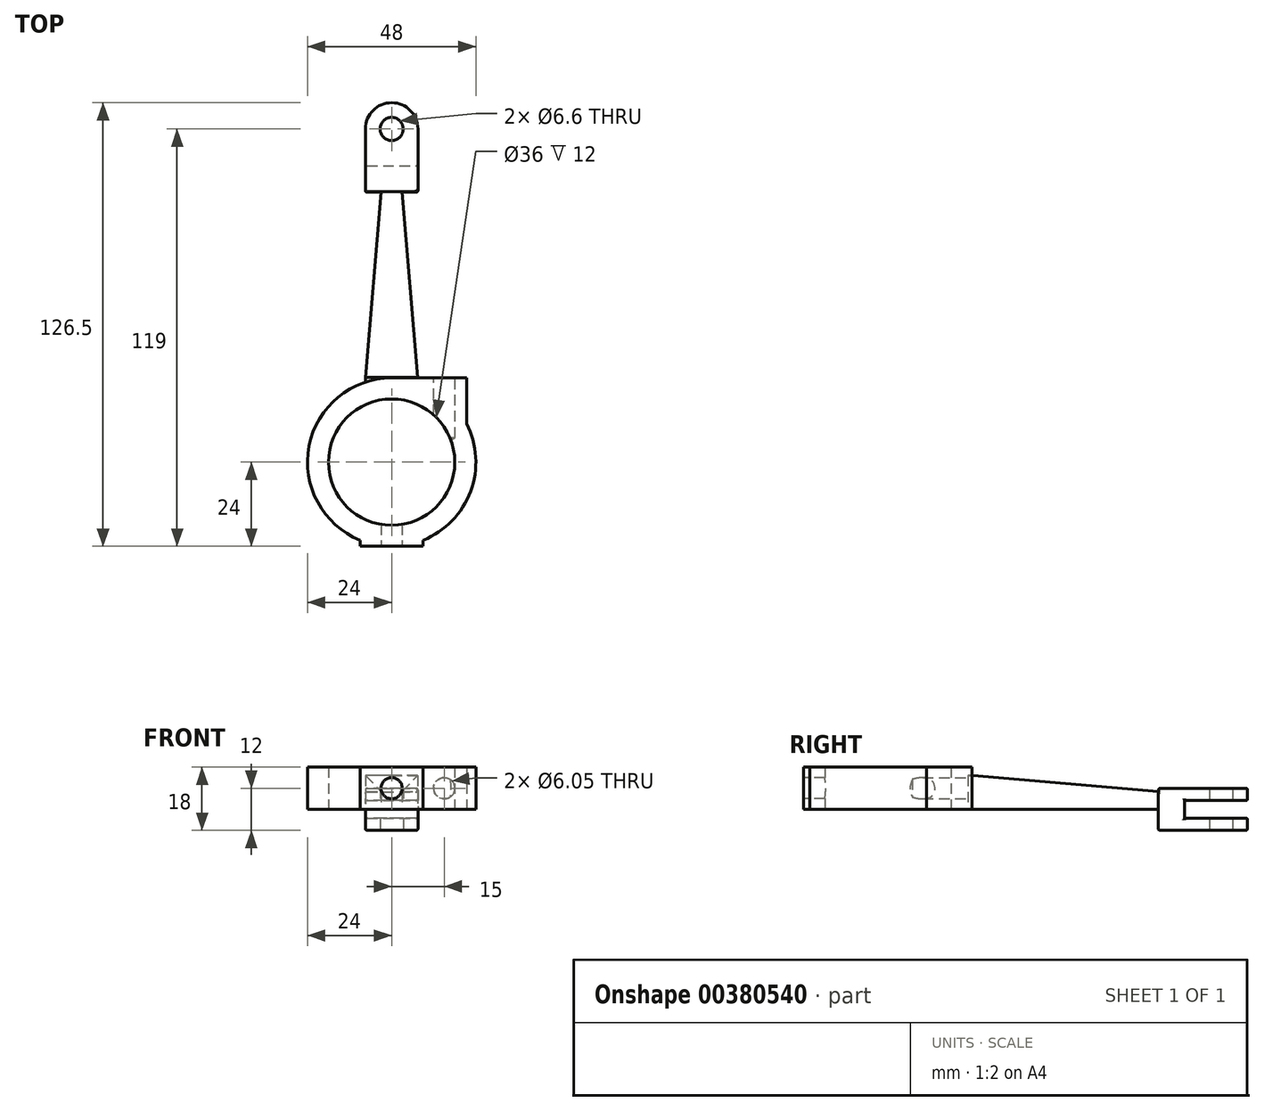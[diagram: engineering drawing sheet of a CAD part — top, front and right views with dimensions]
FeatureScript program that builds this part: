
annotation { "Feature Type Name" : "Feature", "Feature Type Description" : "" }
export const myFeature = defineFeature(function(context is Context, id is Id, definition is map)
    precondition{}
    {
        {
            var Q0;
            Q0=qCreatedBy(makeId("Top.planeOp"),FACE);
            var sketch = newSketch(context, id + "F0", { "sketchPlane" : qUnion([Q0])});
            skCircle(sketch, "E0", {"center": v(0, 0) * mm, "radius": 18 * mm});
            skArc(sketch, "E1", {"start": v(9, -22.25) * mm, "mid": v(22.5, -8.35) * mm, "end": v(21.33, 11) * mm});
            skLineSegment(sketch, "E2", {"start": v(-7.5, 22.8) * mm, "end": v(-3, 77) * mm});
            skLineSegment(sketch, "E3", {"start": v(3, 77) * mm, "end": v(7.4, 24) * mm});
            skLineSegment(sketch, "E4.bottom", {"start": v(-7.5, 95) * mm, "end": v(7.5, 95) * mm, "construction": true});
            skLineSegment(sketch, "E4.left", {"start": v(-7.5, 95) * mm, "end": v(-7.5, 77) * mm});
            skLineSegment(sketch, "E4.right", {"start": v(7.5, 95) * mm, "end": v(7.5, 77) * mm});
            skLineSegment(sketch, "E5", {"start": v(-7.5, 77) * mm, "end": v(-3, 77) * mm});
            skLineSegment(sketch, "E6", {"start": v(3, 77) * mm, "end": v(7.5, 77) * mm});
            skArc(sketch, "E7", {"start": v(7.5, 95) * mm, "mid": v(0, 102.5) * mm, "end": v(-7.5, 95) * mm});
            skCircle(sketch, "E8", {"center": v(0, 95) * mm, "radius": 3.3 * mm});
            skLineSegment(sketch, "E9", {"start": v(0, 24) * mm, "end": v(0, 77) * mm, "construction": true});
            skLineSegment(sketch, "E10", {"start": v(-7.5, 77) * mm, "end": v(7.5, 77) * mm});
            skLineSegment(sketch, "E11", {"start": v(0, 0) * mm, "end": v(0, 95) * mm, "construction": true});
            skLineSegment(sketch, "E12", {"start": v(-9, -22.25) * mm, "end": v(-9, -24) * mm});
            skLineSegment(sketch, "E13", {"start": v(9, -22.25) * mm, "end": v(9, -24) * mm});
            skLineSegment(sketch, "E14", {"start": v(21.33, 11) * mm, "end": v(21.33, 24) * mm});
            skLineSegment(sketch, "E15", {"start": v(21.33, 24) * mm, "end": v(7.4, 24) * mm});
            skLineSegment(sketch, "E16", {"start": v(-9, -24) * mm, "end": v(9, -24) * mm});
            skArc(sketch, "E17.trimOffspring", {"start": v(0, 24) * mm, "mid": v(-23.56, 4.58) * mm, "end": v(-9, -22.25) * mm});
            skLineSegment(sketch, "E18", {"start": v(0, 24) * mm, "end": v(7.4, 24) * mm});
            skSolve(sketch);
        }
        {
            var Q0;
            Q0=makeQuery(id+"F0.imprint","IMPRINT",FACE,{"disambiguationData":[TD([[makeQuery(id+"F0.imprint","IMPRINT",EDGE,{"derivedFrom":sQuery(id+"F0.wireOp",EDGE,"E0")}),-1.0]])]});
            extrude(context, id + "F1", {"entities" : qUnion([Q0]), "depth" : 12 * mm});
        }
        {
            var Q0;
            {var subQ1=sQuery(id+"F0.wireOp",EDGE,"E2");Q0=makeQuery(id+"F0.imprint","IMPRINT",FACE,{"disambiguationData":[TD([[makeQuery(id+"F0.imprint","IMPRINT",EDGE,{"derivedFrom":subQ1}),-1.0]])]});}
            extrude(context, id + "F2", {"entities" : qUnion([Q0]), "operationType" : NewBodyOperationType.ADD, "depth" : 9.6 * mm});
        }
        {
            var Q0;
            {var subQ1=sQuery(id+"F0.wireOp",EDGE,"E4.left");Q0=makeQuery(id+"F0.imprint","IMPRINT",FACE,{"disambiguationData":[TD([[makeQuery(id+"F0.imprint","IMPRINT",EDGE,{"derivedFrom":subQ1}),1.0]])]});}
            extrude(context, id + "F3", {"entities" : qUnion([Q0]), "operationType" : NewBodyOperationType.ADD, "depth" : 6 * mm, "hasSecondDirection" : true, "secondDirectionOppositeDirection" : true, "secondDirectionDepth" : 6 * mm});
        }
        {
            var Q0;
            Q0=qCreatedBy(makeId("Right.planeOp"),FACE);
            var sketch = newSketch(context, id + "F4", { "sketchPlane" : qUnion([Q0])});
            skLineSegment(sketch, "E19", {"start": v(77.12, 5) * mm, "end": v(24.03, 9.61) * mm});
            skLineSegment(sketch, "E20", {"start": v(24.03, 9.61) * mm, "end": v(77.12, 9.61) * mm});
            skLineSegment(sketch, "E21", {"start": v(77.12, 9.61) * mm, "end": v(77.12, 5) * mm});
            skSolve(sketch);
        }
        {
            var Q0;
            Q0=qSketchRegion(id+"F4",true);
            extrude(context, id + "F5", {"entities" : qUnion([Q0]), "operationType" : NewBodyOperationType.REMOVE, "oppositeDirection" : true, "depth" : 25 * mm, "hasSecondDirection" : true, "secondDirectionOppositeDirection" : false, "secondDirectionDepth" : 25 * mm});
        }
        {
            var Q0;
            Q0=makeQuery(id+"F3.opExtrude","SWEPT_FACE",FACE,{"disambiguationData":[OSD([sQuery(id+"F0.wireOp",EDGE,"E4.right")])]});
            var sketch = newSketch(context, id + "F6", { "sketchPlane" : qUnion([Q0])});
            skLineSegment(sketch, "E22.bottom", {"start": v(102.5, -2.5) * mm, "end": v(84.5, -2.5) * mm});
            skLineSegment(sketch, "E22.top", {"start": v(102.5, 2.5) * mm, "end": v(84.5, 2.5) * mm});
            skLineSegment(sketch, "E22.left", {"start": v(102.5, -2.5) * mm, "end": v(102.5, 2.5) * mm});
            skLineSegment(sketch, "E22.right", {"start": v(84.5, -2.5) * mm, "end": v(84.5, 2.5) * mm});
            skPoint(sketch, "E22.middle", {"position": v(93.5, 0) * mm});
            skSolve(sketch);
        }
        {
            var Q0;
            {var subQ0=sQuery(id+"F6.wireOp",EDGE,"E22.right");Q0=makeQuery(id+"F6.imprint","IMPRINT",FACE,{"disambiguationData":[TD([[makeQuery(id+"F6.imprint","IMPRINT",EDGE,{"derivedFrom":subQ0}),-1.0]])]});}
            var Q1;
            {var subQ0=sQuery(id+"F6.wireOp",EDGE,"E22.left");Q1=makeQuery(id+"F6.imprint","IMPRINT",FACE,{"disambiguationData":[TD([[makeQuery(id+"F6.imprint","IMPRINT",EDGE,{"derivedFrom":subQ0}),1.0]])]});}
            extrude(context, id + "F7", {"entities" : qUnion([Q0, Q1]), "operationType" : NewBodyOperationType.REMOVE, "oppositeDirection" : true, "depth" : 25 * mm});
        }
        {
            var Q0;
            Q0=makeQuery(id+"F1.opExtrude","SWEPT_FACE",FACE,{"disambiguationData":[OSD([sQuery(id+"F0.wireOp",EDGE,"E16")])]});
            var sketch = newSketch(context, id + "F8", { "sketchPlane" : qUnion([Q0])});
            skLineSegment(sketch, "E23", {"start": v(0, 0) * mm, "end": v(0, 12) * mm, "construction": true});
            skLineSegment(sketch, "E24", {"start": v(9, 6) * mm, "end": v(-9, 6) * mm, "construction": true});
            skPoint(sketch, "E25", {"position": v(0, 6) * mm});
            skSolve(sketch);
        }
        {
            var Q0;
            Q0=sQuery(id+"F8.wireOp",VERTEX,"E25");
            var Q1;
            Q1=makeQuery(id+"F1.opExtrude","SWEPT_BODY",BODY,{"disambiguationData":[OSD([sQuery(id+"F0.wireOp",EDGE,"E0"),sQuery(id+"F0.wireOp",EDGE,"E1"),sQuery(id+"F0.wireOp",EDGE,"E12"),sQuery(id+"F0.wireOp",EDGE,"E13"),sQuery(id+"F0.wireOp",EDGE,"E14"),sQuery(id+"F0.wireOp",EDGE,"E15"),sQuery(id+"F0.wireOp",EDGE,"E16"),sQuery(id+"F0.wireOp",EDGE,"E17.trimOffspring"),sQuery(id+"F0.wireOp",EDGE,"E18")])]});
            hole(context, id + "F9", {"style" : HoleStyle.SIMPLE, "endStyle" : HoleEndStyle.BLIND, "holeDiameter" : 5 * mm, "holeDepth" : 17 * mm, "tappedDepth" : 12.7 * mm, "tapClearance" : 3, "locations" : qUnion([Q0]), "scope" : qUnion([Q1])});
        }
        {
            var Q0;
            Q0=makeQuery(id+"F1.opExtrude","SWEPT_FACE",FACE,{"disambiguationData":[OSD([sQuery(id+"F0.wireOp",EDGE,"E15"),sQuery(id+"F0.wireOp",EDGE,"E18")])]});
            var sketch = newSketch(context, id + "F10", { "sketchPlane" : qUnion([Q0])});
            skLineSegment(sketch, "E26", {"start": v(-21.33, 6) * mm, "end": v(0, 6) * mm, "construction": true});
            skLineSegment(sketch, "E27", {"start": v(-15, 21.84) * mm, "end": v(-15, -13.14) * mm, "construction": true});
            skPoint(sketch, "E28", {"position": v(-15, 6) * mm});
            skSolve(sketch);
        }
        {
            var Q0;
            Q0=sQuery(id+"F10.wireOp",VERTEX,"E28");
            var Q1;
            Q1=makeQuery(id+"F1.opExtrude","SWEPT_BODY",BODY,{"disambiguationData":[OSD([sQuery(id+"F0.wireOp",EDGE,"E0"),sQuery(id+"F0.wireOp",EDGE,"E1"),sQuery(id+"F0.wireOp",EDGE,"E12"),sQuery(id+"F0.wireOp",EDGE,"E13"),sQuery(id+"F0.wireOp",EDGE,"E14"),sQuery(id+"F0.wireOp",EDGE,"E15"),sQuery(id+"F0.wireOp",EDGE,"E16"),sQuery(id+"F0.wireOp",EDGE,"E17.trimOffspring"),sQuery(id+"F0.wireOp",EDGE,"E18")])]});
            hole(context, id + "F11", {"style" : HoleStyle.SIMPLE, "endStyle" : HoleEndStyle.BLIND, "holeDiameter" : 5 * mm, "holeDepth" : 17 * mm, "tappedDepth" : 12.7 * mm, "tapClearance" : 3, "locations" : qUnion([Q0]), "scope" : qUnion([Q1])});
        }
        {
            var Q0;
            Q0=sQuery(id+"F10.wireOp",VERTEX,"E28");
            var Q1;
            Q1=makeQuery(id+"F1.opExtrude","SWEPT_BODY",BODY,{"disambiguationData":[OSD([sQuery(id+"F0.wireOp",EDGE,"E0"),sQuery(id+"F0.wireOp",EDGE,"E1"),sQuery(id+"F0.wireOp",EDGE,"E12"),sQuery(id+"F0.wireOp",EDGE,"E13"),sQuery(id+"F0.wireOp",EDGE,"E14"),sQuery(id+"F0.wireOp",EDGE,"E15"),sQuery(id+"F0.wireOp",EDGE,"E16"),sQuery(id+"F0.wireOp",EDGE,"E17.trimOffspring"),sQuery(id+"F0.wireOp",EDGE,"E18")])]});
            hole(context, id + "F12", {"style" : HoleStyle.SIMPLE, "endStyle" : HoleEndStyle.BLIND, "holeDiameter" : 6.05 * mm, "holeDepth" : 17 * mm, "tappedDepth" : 12.7 * mm, "tapClearance" : 3, "locations" : qUnion([Q0]), "scope" : qUnion([Q1])});
        }
        {
            var Q0;
            Q0=sQuery(id+"F8.wireOp",VERTEX,"E25");
            var Q1;
            Q1=makeQuery(id+"F1.opExtrude","SWEPT_BODY",BODY,{"disambiguationData":[OSD([sQuery(id+"F0.wireOp",EDGE,"E0"),sQuery(id+"F0.wireOp",EDGE,"E1"),sQuery(id+"F0.wireOp",EDGE,"E12"),sQuery(id+"F0.wireOp",EDGE,"E13"),sQuery(id+"F0.wireOp",EDGE,"E14"),sQuery(id+"F0.wireOp",EDGE,"E15"),sQuery(id+"F0.wireOp",EDGE,"E16"),sQuery(id+"F0.wireOp",EDGE,"E17.trimOffspring"),sQuery(id+"F0.wireOp",EDGE,"E18")])]});
            hole(context, id + "F13", {"style" : HoleStyle.SIMPLE, "endStyle" : HoleEndStyle.BLIND, "holeDiameter" : 6.05 * mm, "holeDepth" : 17 * mm, "tappedDepth" : 12.7 * mm, "tapClearance" : 3, "locations" : qUnion([Q0]), "scope" : qUnion([Q1])});
        }
        {
            var Q0;
            Q0=makeQuery(id+"F7.boolean.opBoolean","INTERSECT",EDGE,{"derivedFrom":[makeQuery(id+"F3.opExtrude","SWEPT_FACE",FACE,{"disambiguationData":[OSD([sQuery(id+"F0.wireOp",EDGE,"E7")])]}),makeQuery(id+"F7.opExtrude","SWEPT_FACE",FACE,{"disambiguationData":[OSD([sQuery(id+"F6.wireOp",EDGE,"E22.bottom")])]})]});
            var Q1;
            Q1=makeQuery(id+"F7.boolean.opBoolean","INTERSECT",EDGE,{"derivedFrom":[makeQuery(id+"F3.opExtrude","SWEPT_FACE",FACE,{"disambiguationData":[OSD([sQuery(id+"F0.wireOp",EDGE,"E7")])]}),makeQuery(id+"F7.opExtrude","SWEPT_FACE",FACE,{"disambiguationData":[OSD([sQuery(id+"F6.wireOp",EDGE,"E22.top")])]})]});
            var Q2;
            Q2=makeQuery(id+"F3.opExtrude","CAP_EDGE",EDGE,{"disambiguationData":[OSD([sQuery(id+"F0.wireOp",EDGE,"E7")])],"isStart":false});
            var Q3;
            Q3=makeQuery(id+"F3.opExtrude","CAP_EDGE",EDGE,{"disambiguationData":[OSD([sQuery(id+"F0.wireOp",EDGE,"E7")])],"isStart":true});
            var Q4;
            Q4=makeQuery(id+"F7.boolean.opBoolean","INTERSECT",EDGE,{"derivedFrom":[makeQuery(id+"F3.opExtrude","SWEPT_FACE",FACE,{"disambiguationData":[OSD([sQuery(id+"F0.wireOp",EDGE,"E4.left")])]}),makeQuery(id+"F7.opExtrude","SWEPT_FACE",FACE,{"disambiguationData":[OSD([sQuery(id+"F6.wireOp",EDGE,"E22.right")])]})]});
            var Q5;
            Q5=makeQuery(id+"F3.opExtrude","SWEPT_FACE",FACE,{"disambiguationData":[OSD([sQuery(id+"F0.wireOp",EDGE,"E4.left")])]});
            var Q6;
            Q6=makeQuery(id+"F3.opExtrude","CAP_EDGE",EDGE,{"disambiguationData":[OSD([sQuery(id+"F0.wireOp",EDGE,"E10")])],"isStart":true});
            var Q7;
            Q7=makeQuery(id+"F3.opExtrude","CAP_EDGE",EDGE,{"disambiguationData":[OSD([sQuery(id+"F0.wireOp",EDGE,"E4.right")])],"isStart":true});
            var Q8;
            Q8=makeQuery(id+"F3.opExtrude","SWEPT_EDGE",EDGE,{"disambiguationData":[OSD([sQuery(id+"F0.wireOp",EDGE,"E4.right"),sQuery(id+"F0.wireOp",EDGE,"E10")])]});
            var Q9;
            Q9=makeQuery(id+"F3.opExtrude","CAP_EDGE",EDGE,{"disambiguationData":[OSD([sQuery(id+"F0.wireOp",EDGE,"E4.right")])],"isStart":false});
            var Q10;
            Q10=makeQuery(id+"F7.boolean.opBoolean","COPY",EDGE,{"derivedFrom":makeQuery(id+"F7.opExtrude","CAP_EDGE",EDGE,{"disambiguationData":[OSD([sQuery(id+"F6.wireOp",EDGE,"E22.right")])],"isStart":true})});
            var Q11;
            Q11=makeQuery(id+"F5.boolean.opBoolean","INTERSECT",EDGE,{"derivedFrom":[makeQuery(id+"F3.opExtrude","CAP_FACE",FACE,{"disambiguationData":[OSD([sQuery(id+"F0.wireOp",EDGE,"E4.left"),sQuery(id+"F0.wireOp",EDGE,"E4.right"),sQuery(id+"F0.wireOp",EDGE,"E7"),sQuery(id+"F0.wireOp",EDGE,"E8"),sQuery(id+"F0.wireOp",EDGE,"E10")])],"isStart":false}),makeQuery(id+"F5.opExtrude","SWEPT_FACE",FACE,{"disambiguationData":[OSD([sQuery(id+"F4.wireOp",EDGE,"E21")])]})]});
            fillet(context, id + "F14", {"entities" : qUnion([Q0, Q1, Q2, Q3, Q4, Q5, Q6, Q7, Q8, Q9, Q10, Q11]), "radius" : .5 * mm, "tangentPropagation" : true, "allowEdgeOverflow" : false});
        }
    });
